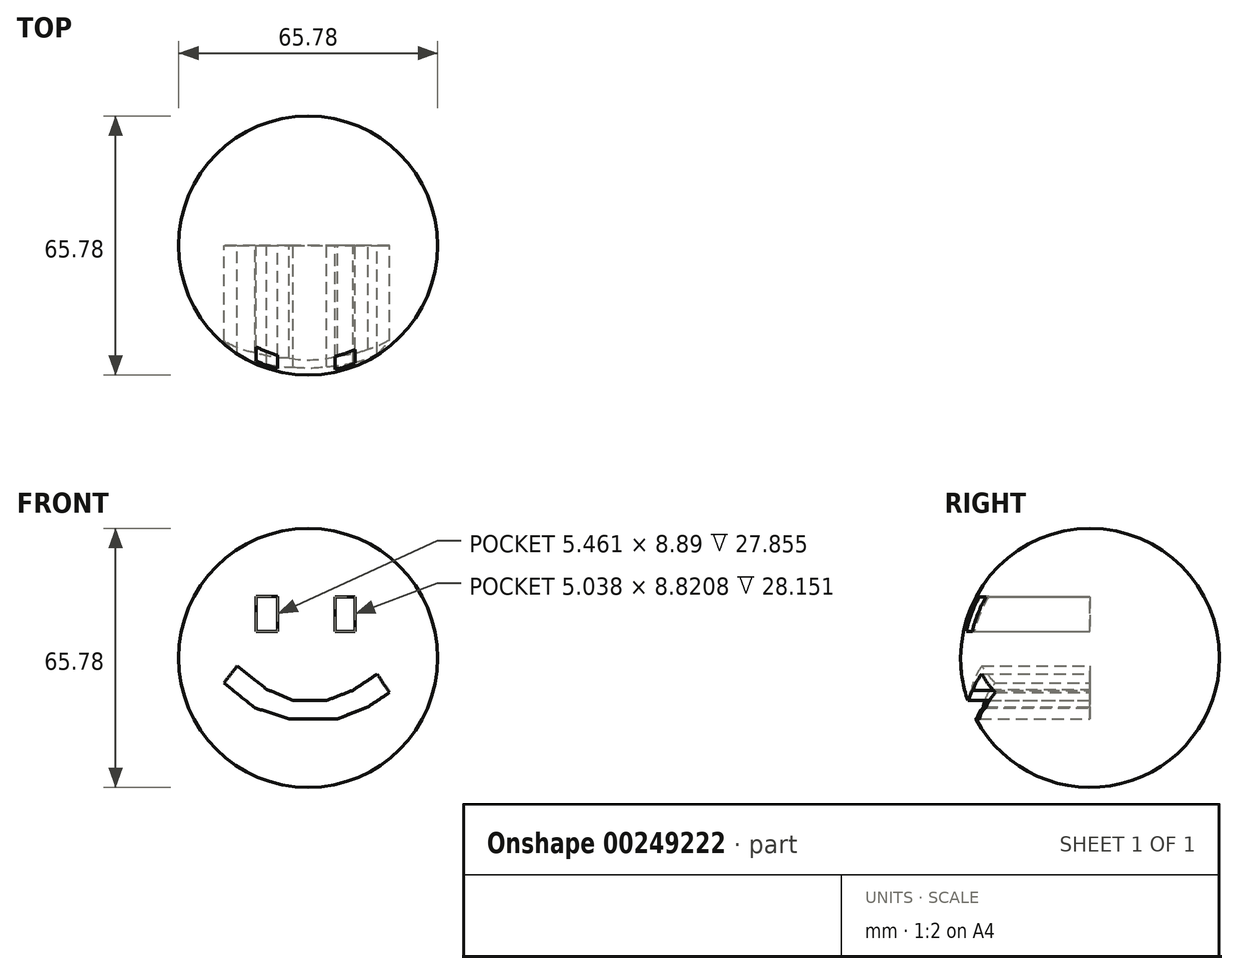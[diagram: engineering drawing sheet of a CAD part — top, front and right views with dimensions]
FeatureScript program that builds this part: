
annotation { "Feature Type Name" : "Feature", "Feature Type Description" : "" }
export const myFeature = defineFeature(function(context is Context, id is Id, definition is map)
    precondition{}
    {
        {
            var Q0;
            Q0=qCreatedBy(makeId("Top.planeOp"),FACE);
            var sketch = newSketch(context, id + "F0", { "sketchPlane" : qUnion([Q0])});
            skArc(sketch, "E0", {"start": v(0, -32.9) * mm, "mid": v(32.9, 0) * mm, "end": v(0, 32.9) * mm});
            skLineSegment(sketch, "E1", {"start": v(0, 32.9) * mm, "end": v(0, -32.9) * mm});
            skSolve(sketch);
        }
        {
            var Q0;
            Q0=makeQuery(id+"F0.imprint","IMPRINT",FACE,{"disambiguationData":[TD([[makeQuery(id+"F0.imprint","IMPRINT",EDGE,{"derivedFrom":sQuery(id+"F0.wireOp",EDGE,"E0")}),1.0]])]});
            var Q1;
            Q1=sQuery(id+"F0.wireOp",EDGE,"E1");
            revolve(context, id + "F1", {"entities" : qUnion([Q0]), "axis" : qUnion([Q1]), "revolveType" : RevolveType.FULL});
        }
        {
            var Q0;
            Q0=qCreatedBy(makeId("Front.planeOp"),FACE);
            var sketch = newSketch(context, id + "F2", { "sketchPlane" : qUnion([Q0])});
            skLineSegment(sketch, "E2", {"start": v(-13.22, 15.68) * mm, "end": v(-7.76, 15.68) * mm});
            skLineSegment(sketch, "E3", {"start": v(-7.76, 15.68) * mm, "end": v(-7.76, 6.8) * mm});
            skLineSegment(sketch, "E4", {"start": v(-13.22, 6.8) * mm, "end": v(-7.76, 6.8) * mm});
            skLineSegment(sketch, "E5", {"start": v(-13.22, 6.8) * mm, "end": v(-13.22, 15.68) * mm});
            skSolve(sketch);
        }
        {
            var Q0;
            Q0 = qSketchRegion(id + "F2", true);
            extrude(context, id + "F3", {"entities" : qUnion([Q0]), "operationType" : NewBodyOperationType.REMOVE, "endBound" : BoundingType.THROUGH_ALL, "depth" : 127 * mm});
        }
        {
            var Q0;
            Q0=qCreatedBy(makeId("Front.planeOp"),FACE);
            var sketch = newSketch(context, id + "F4", { "sketchPlane" : qUnion([Q0])});
            skLineSegment(sketch, "E6", {"start": v(6.9, 15.56) * mm, "end": v(6.9, 6.74) * mm});
            skLineSegment(sketch, "E7", {"start": v(6.9, 6.74) * mm, "end": v(11.93, 6.74) * mm});
            skLineSegment(sketch, "E8", {"start": v(11.93, 6.74) * mm, "end": v(11.93, 15.55) * mm});
            skLineSegment(sketch, "E9", {"start": v(11.93, 15.55) * mm, "end": v(6.9, 15.56) * mm});
            skSolve(sketch);
        }
        {
            var Q0;
            Q0 = qSketchRegion(id + "F4", true);
            extrude(context, id + "F5", {"entities" : qUnion([Q0]), "operationType" : NewBodyOperationType.REMOVE, "endBound" : BoundingType.THROUGH_ALL, "depth" : 18.6 * mm});
        }
        {
            var Q0;
            Q0=qCreatedBy(makeId("Front.planeOp"),FACE);
            var sketch = newSketch(context, id + "F6", { "sketchPlane" : qUnion([Q0])});
            skLineSegment(sketch, "E10", {"start": v(-17.99, -2) * mm, "end": v(-10.55, -7.95) * mm});
            skLineSegment(sketch, "E11", {"start": v(-10.55, -7.95) * mm, "end": v(-3.88, -10.8) * mm});
            skLineSegment(sketch, "E12", {"start": v(-3.88, -10.8) * mm, "end": v(4.74, -10.8) * mm});
            skLineSegment(sketch, "E13", {"start": v(4.74, -10.8) * mm, "end": v(11.4, -8.2) * mm});
            skLineSegment(sketch, "E14", {"start": v(11.4, -8.2) * mm, "end": v(17.52, -4.1) * mm});
            skLineSegment(sketch, "E15", {"start": v(17.52, -4.1) * mm, "end": v(20.66, -8.8) * mm});
            skLineSegment(sketch, "E16", {"start": v(20.66, -8.8) * mm, "end": v(15.17, -12.46) * mm});
            skLineSegment(sketch, "E17", {"start": v(15.17, -12.46) * mm, "end": v(7.46, -15.46) * mm});
            skLineSegment(sketch, "E18", {"start": v(7.46, -15.46) * mm, "end": v(-4.9, -15.46) * mm});
            skLineSegment(sketch, "E19", {"start": v(-4.9, -15.46) * mm, "end": v(-13.52, -12.67) * mm});
            skLineSegment(sketch, "E20", {"start": v(-13.52, -12.67) * mm, "end": v(-21.41, -6.36) * mm});
            skLineSegment(sketch, "E21", {"start": v(-21.41, -6.36) * mm, "end": v(-17.99, -2) * mm});
            skSolve(sketch);
        }
        {
            var Q0;
            Q0 = qSketchRegion(id + "F6", true);
            extrude(context, id + "F7", {"entities" : qUnion([Q0]), "operationType" : NewBodyOperationType.REMOVE, "endBound" : BoundingType.THROUGH_ALL, "depth" : 25.4 * mm});
        }
    });
